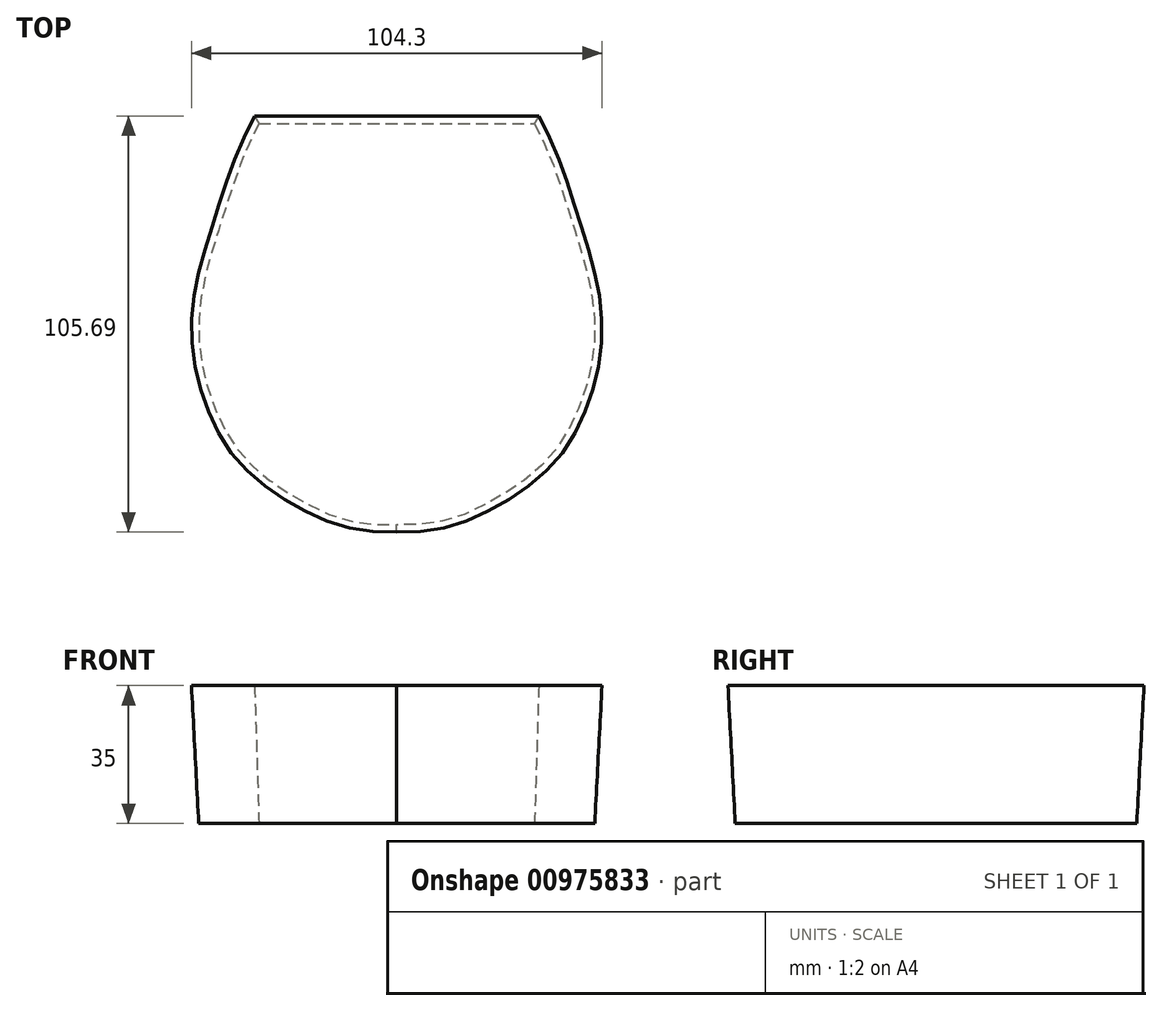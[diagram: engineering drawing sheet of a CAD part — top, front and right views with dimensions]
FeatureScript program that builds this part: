
annotation { "Feature Type Name" : "Feature", "Feature Type Description" : "" }
export const myFeature = defineFeature(function(context is Context, id is Id, definition is map)
    precondition{}
    {
        {
            var Q0;
            Q0=qCreatedBy(makeId("Top.planeOp"),FACE);
            var sketch = newSketch(context, id + "F0", { "sketchPlane" : qUnion([Q0])});
            skLineSegment(sketch, "E0", {"start": v(0, 66.67) * mm, "end": v(0, -83.92) * mm, "construction": true});
            skLineSegment(sketch, "E1", {"start": v(-85.24, 0) * mm, "end": v(78.22, 0) * mm, "construction": true});
            skLineSegment(sketch, "E2", {"start": v(0, 48.25) * mm, "end": v(35, 48.25) * mm});
            skFitSpline(sketch, "E3", {"points": [v(35, 48.25) * mm, v(40.51, 35.6) * mm, v(45.46, 20.48) * mm, v(49.3, 6.19) * mm, v(49.86, -10.86) * mm, v(43.81, -29.28) * mm, v(35, -40.27) * mm, v(20.44, -49.62) * mm, v(0, -53.74) * mm], "startDerivative": vector(65.42, -123.14) * mm, "endDerivative": vector(-202.13, 5.88) * mm});
            skLineSegment(sketch, "E4.1", {"start": v(0, 44.25) * mm, "end": v(31.44, 44.25) * mm});
            skLineSegment(sketch, "E5.MirrorCS", {"start": v(0, 21.84) * mm, "end": v(0, 172.43) * mm, "construction": true});
            skLineSegment(sketch, "E6.MirrorCS", {"start": v(0, 44.25) * mm, "end": v(-31.44, 44.25) * mm});
            skFitSpline(sketch, "E7.MirrorCS", {"points": [v(-35, 48.25) * mm, v(-40.51, 35.6) * mm, v(-45.46, 20.48) * mm, v(-49.3, 6.19) * mm, v(-49.86, -10.86) * mm, v(-43.81, -29.28) * mm, v(-35, -40.27) * mm, v(-20.44, -49.62) * mm, v(0, -53.74) * mm], "startDerivative": vector(-65.42, -123.14) * mm, "endDerivative": vector(202.13, 5.88) * mm});
            skLineSegment(sketch, "E8.MirrorCS", {"start": v(0, 48.25) * mm, "end": v(-35, 48.25) * mm});
            skFitSpline(sketch, "E9.0", {"points": [v(-30.58, 45.9) * mm, v(-31.23, 44.68) * mm, v(-32.38, 42.41) * mm, v(-33.54, 39.8) * mm, v(-34.4, 37.7) * mm, v(-35, 36.11) * mm, v(-35.61, 34.46) * mm, v(-36.23, 32.7) * mm, v(-36.86, 30.89) * mm, v(-37.7, 28.38) * mm, v(-38.75, 25.14) * mm, v(-39.79, 21.85) * mm, v(-40.6, 19.25) * mm, v(-41.4, 16.7) * mm, v(-42.34, 13.64) * mm, v(-43.34, 10.08) * mm, v(-44.04, 7.14) * mm, v(-44.5, 4.74) * mm, v(-44.9, 2.3) * mm, v(-45.24, -0.8) * mm, v(-45.37, -4.63) * mm, v(-45.2, -7.88) * mm, v(-44.87, -10.51) * mm, v(-44.52, -12.53) * mm, v(-44.07, -14.58) * mm, v(-43.35, -17.3) * mm, v(-42.25, -20.67) * mm, v(-40.94, -23.83) * mm, v(-39.81, -26.16) * mm, v(-38.95, -27.77) * mm, v(-38.06, -29.26) * mm, v(-36.83, -31.1) * mm, v(-35.52, -32.76) * mm, v(-34.05, -34.34) * mm, v(-32.86, -35.5) * mm, v(-31.56, -36.65) * mm, v(-30.13, -37.81) * mm, v(-28.6, -38.97) * mm, v(-26.45, -40.48) * mm, v(-23.6, -42.29) * mm, v(-20.95, -43.76) * mm, v(-19.19, -44.67) * mm, v(-18.3, -45.1) * mm, v(-17.44, -45.51) * mm, v(-16.3, -46.02) * mm, v(-14.92, -46.6) * mm, v(-12.68, -47.4) * mm, v(-9.75, -48.18) * mm, v(-5.58, -48.73) * mm, v(-2.1, -48.8) * mm, v(-0.15, -48.74) * mm]});
            skFitSpline(sketch, "E10.0", {"points": [v(30.58, 45.9) * mm, v(31.23, 44.68) * mm, v(32.38, 42.41) * mm, v(33.54, 39.8) * mm, v(34.4, 37.7) * mm, v(35, 36.11) * mm, v(35.61, 34.46) * mm, v(36.23, 32.7) * mm, v(36.86, 30.89) * mm, v(37.7, 28.38) * mm, v(38.75, 25.14) * mm, v(39.79, 21.85) * mm, v(40.6, 19.25) * mm, v(41.4, 16.7) * mm, v(42.34, 13.64) * mm, v(43.34, 10.08) * mm, v(44.04, 7.14) * mm, v(44.5, 4.74) * mm, v(44.9, 2.3) * mm, v(45.24, -0.8) * mm, v(45.37, -4.63) * mm, v(45.2, -7.88) * mm, v(44.87, -10.51) * mm, v(44.52, -12.53) * mm, v(44.07, -14.58) * mm, v(43.35, -17.3) * mm, v(42.25, -20.67) * mm, v(40.94, -23.83) * mm, v(39.81, -26.16) * mm, v(38.95, -27.77) * mm, v(38.06, -29.26) * mm, v(36.83, -31.1) * mm, v(35.52, -32.76) * mm, v(34.05, -34.34) * mm, v(32.86, -35.5) * mm, v(31.56, -36.65) * mm, v(30.13, -37.81) * mm, v(28.6, -38.97) * mm, v(26.45, -40.48) * mm, v(23.6, -42.29) * mm, v(20.95, -43.76) * mm, v(19.19, -44.67) * mm, v(18.3, -45.1) * mm, v(17.44, -45.51) * mm, v(16.3, -46.02) * mm, v(14.92, -46.6) * mm, v(12.68, -47.4) * mm, v(9.75, -48.18) * mm, v(5.58, -48.73) * mm, v(2.1, -48.8) * mm, v(0.15, -48.74) * mm]});
            skPoint(sketch, "E11.orphan", {"position": v(-32.56, 44.25) * mm});
            skPoint(sketch, "E12.orphan", {"position": v(32.56, 44.25) * mm});
            skFitSpline(sketch, "E13", {"points": [v(-0.15, -48.74) * mm, v(0.15, -48.74) * mm], "startDerivative": vector(0.3, 0) * mm, "endDerivative": vector(0.3, 0) * mm});
            skSolve(sketch);
        }
        {
            var Q0;
            Q0 = qSketchRegion(id + "F0", true);
            extrude(context, id + "F1", {"entities" : qUnion([Q0]), "depth" : 35 * mm, "offsetDistance" : 25 * mm, "hasDraft" : true, "draftAngle" : 3 * degree});
        }
    });
